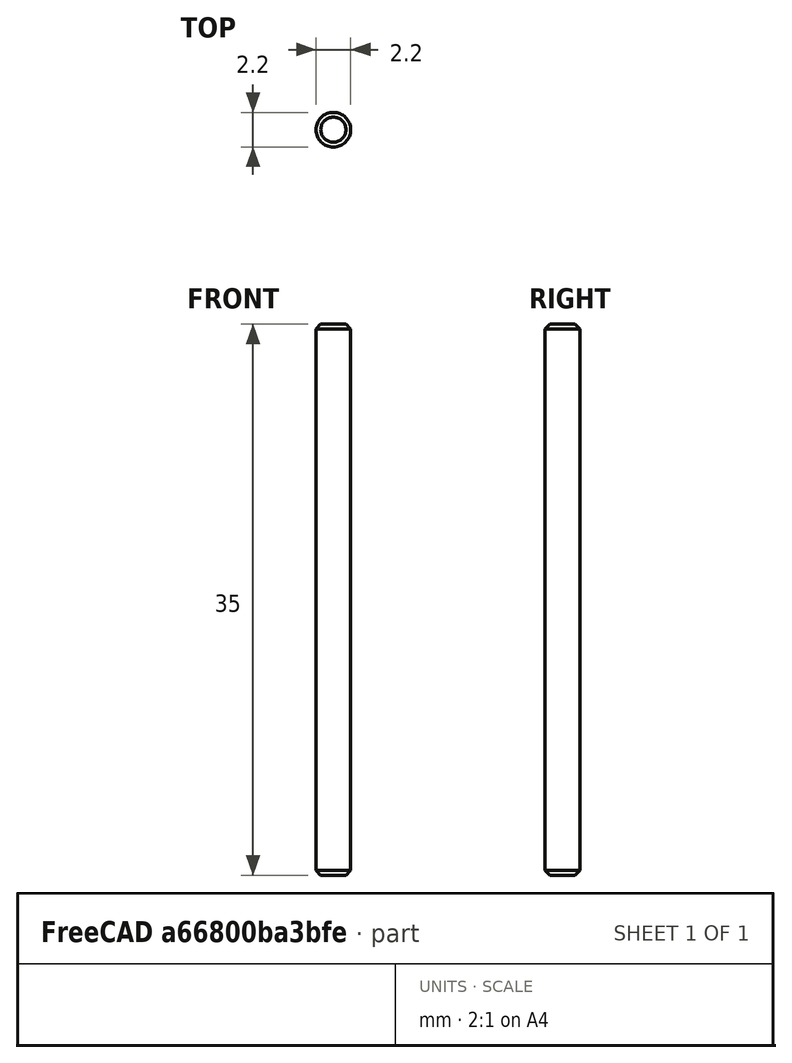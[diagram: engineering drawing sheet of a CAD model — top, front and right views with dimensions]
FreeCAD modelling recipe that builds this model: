
FCSTD DOCUMENT  (FreeCAD 1.0R39319 (Git))
Label: track pinFCStd
License: All rights reserved
LicenseURL: https://en.wikipedia.org/wiki/All_rights_reserved
objects: Sketcher::SketchObject×1, PartDesign::Pad×1, PartDesign::Chamfer×1, PartDesign::Body×1
note: 9 computed .brp shape members not serialized (recipe doc carries the construction recipe); baked Part::Feature solids carry a one-line shape summary decoded from their .brp

FEATURE [Sketcher::SketchObject] Sketch
  ArcFitTolerance = 1e-06
  AttachmentSupport = -> [XY_Plane]
  FullyConstrained = true
  MakeInternals = false
  MapMode = 5
  sketch-geometry (1):
    g0: Circle CenterX=0 CenterY=0 CenterZ=0 NormalX=0 NormalY=0 NormalZ=1 AngleXU=0 Radius=1.1
  constraints (2):
    c: Coincident(g0,g-1)
    c: Diameter(g0) = 2.2
FEATURE [PartDesign::Pad] Pad
  Direction = (0,0,1)
  Length = 35
  Length2 = 10
  Profile = -> Sketch
  ReferenceAxis = -> Sketch [N_Axis]
  Refine = true
  Suppressed = false
  Type = 0
FEATURE [PartDesign::Chamfer] Chamfer
  Angle = 45
  Base = -> Pad [Face2,Face3]
  BaseFeature = -> Pad
  ChamferType = 0
  FlipDirection = false
  Refine = true
  Size = 0.3
  Size2 = 1
  SupportTransform = false
  Suppressed = false
  UseAllEdges = false
FEATURE [PartDesign::Body] Body
  AllowCompound = false
  Group = -> [Sketch,Pad,Chamfer]
  Origin = -> Origin
  Tip = -> Chamfer
